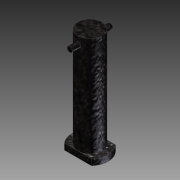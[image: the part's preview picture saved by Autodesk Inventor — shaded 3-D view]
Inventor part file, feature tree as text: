
AUTODESK INVENTOR PART (.ipt)
format: ipt  version: 2012 (Build 160160000, 160)  size: 105,984 bytes
history: native  units: mm
features: extrude x5, sketch x4, fillet x1
ambient origin geometry x8: Origin, YZ Plane, XZ Plane, XY Plane, X Axis, Y Axis, Z Axis, Center Point
bodies: Solid1 (feature_tree)
feature tree (10):
  extrude  "Extrusion1"  Depth=33.0mm TaperAngle=0.0deg
  extrude  "Extrusion2"  Depth=2.0mm TaperAngle=0.0deg
  extrude  "Extrusion3"  Depth=3.0mm TaperAngle=0.0deg
  fillet  "Fillet1"  Radius=2.0mm
  sketch  "Sketch4"  dims[d10=1.75mm d11=30.5mm d12=30.0mm d13=3.0mm d14=0.0mm d15=0.0mm d16=13.4mm d17=0.0mm]
  extrude  "Extrusion4"  Depth=30.5mm
  extrude  "Extrusion5"  Depth=30.0mm TaperAngle=0.0deg
  sketch  "Sketch1"  dims[d0=8.0mm d1=33.0mm d2=0.0mm]
  sketch  "Sketch2"  dims[d3=12.0mm d4=2.0mm d5=0.0mm]
  sketch  "Sketch3"  dims[d6=12.0mm d7=3.0mm d8=0.0mm d9=2.0mm]
